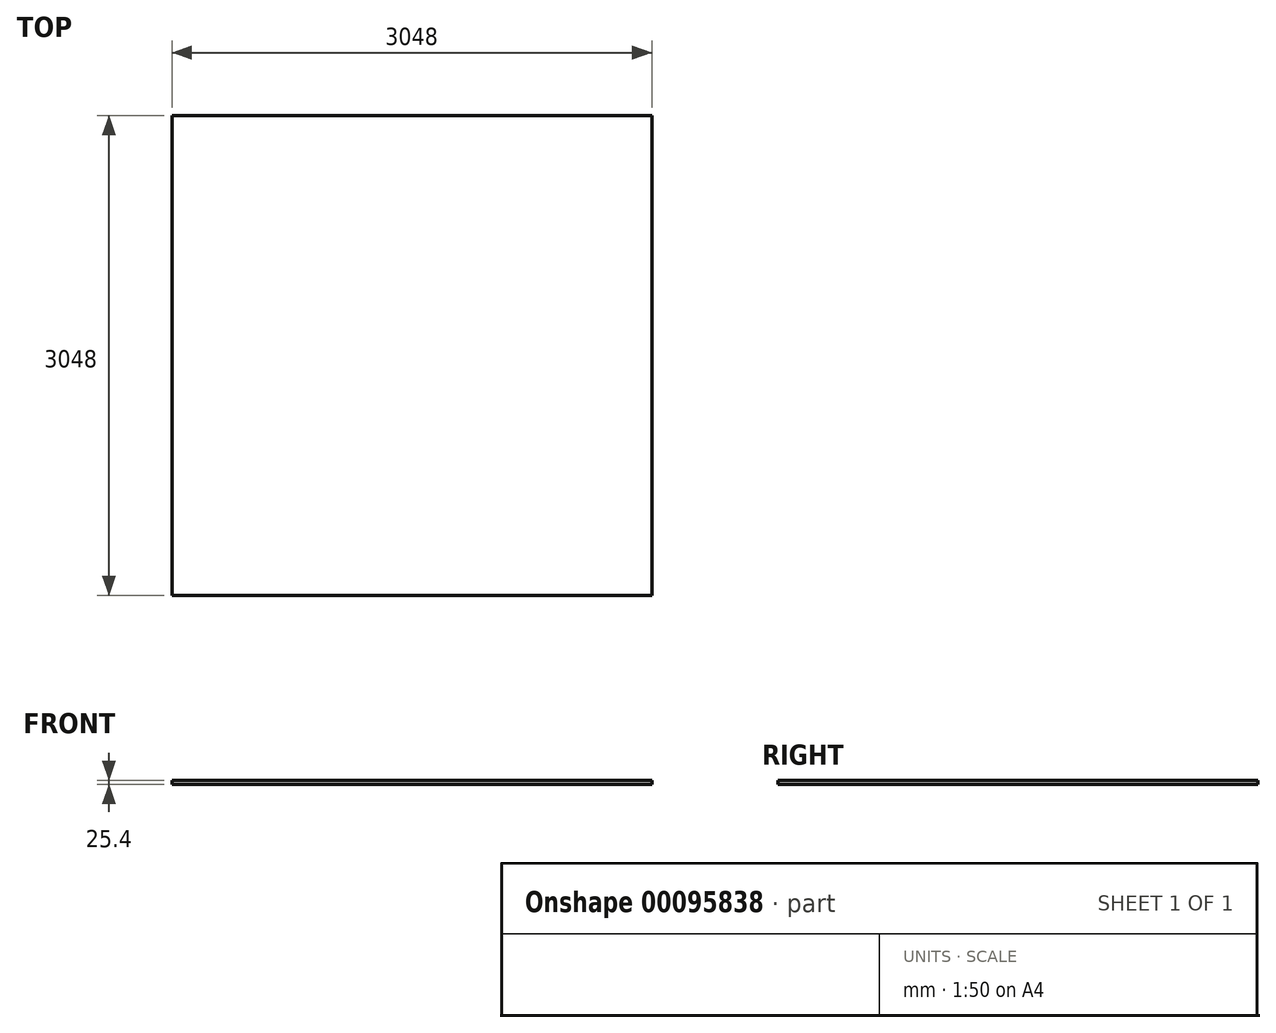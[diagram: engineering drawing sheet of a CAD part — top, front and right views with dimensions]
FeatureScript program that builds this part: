
annotation { "Feature Type Name" : "Feature", "Feature Type Description" : "" }
export const myFeature = defineFeature(function(context is Context, id is Id, definition is map)
    precondition{}
    {
        {
            var Q0;
            Q0=qCreatedBy(makeId("Top.planeOp"),FACE);
            var sketch = newSketch(context, id + "F0", { "sketchPlane" : qUnion([Q0])});
            skLineSegment(sketch, "E0.bottom", {"start": v(-1532.78, 1572.79) * mm, "end": v(1515.22, 1572.79) * mm});
            skLineSegment(sketch, "E0.top", {"start": v(-1532.78, -1475.21) * mm, "end": v(1515.22, -1475.21) * mm});
            skLineSegment(sketch, "E0.left", {"start": v(-1532.78, 1572.79) * mm, "end": v(-1532.78, -1475.21) * mm});
            skLineSegment(sketch, "E0.right", {"start": v(1515.22, 1572.79) * mm, "end": v(1515.22, -1475.21) * mm});
            skSolve(sketch);
        }
        {
            var Q0;
            Q0=qSketchRegion(id+"F0",true);
            extrude(context, id + "F1", {"entities" : qUnion([Q0]), "depth" : 25.4 * mm});
        }
    });
